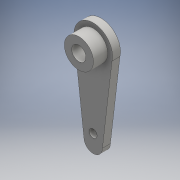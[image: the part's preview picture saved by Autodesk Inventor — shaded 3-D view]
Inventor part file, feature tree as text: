
AUTODESK INVENTOR PART (.ipt)
format: ipt  version: 2016 (Build 200138000, 138)  size: 122,880 bytes
history: native  units: mm
features: sketch x4, extrude x3, hole x1
ambient origin geometry x8: Origin, YZ Plane, XZ Plane, XY Plane, X Axis, Y Axis, Z Axis, Center Point
bodies: Solid1 (feature_tree)
feature tree (8):
  extrude  "Extrusion1"  Depth=5.4mm
  extrude  "Extrusion2"  Depth=5.4mm
  extrude  "Extrusion3"  Depth=3.0mm
  hole  "Hole2"  [1 undecoded]
  sketch  "Sketch1"  dims[d0=5.4mm d1=11.0mm]
  sketch  "Sketch2"  dims[d2=5.4mm d3=0.0mm d4=14.6mm]
  sketch  "Sketch3"  dims[d5=3.0mm d6=0.0mm d7=7.0mm]
  sketch  "Sketch5"  dims[d8=32.0mm d9=3.0mm d10=0.0mm d18=28.89mm d19=3.0mm d20=6.0mm d21=4.0mm d22=2.0mm d23=90.0deg d24=8.0mm d25=20.594885mm]
note: 1 required parameter value undecoded (feature->parameter linkage not recoverable at this tier; creation-order binding heuristic only, values carry confidence <= 0.55)
